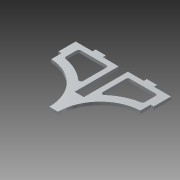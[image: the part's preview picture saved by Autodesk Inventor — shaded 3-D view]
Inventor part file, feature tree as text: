
AUTODESK INVENTOR PART (.ipt)
format: ipt  version: 2013 (Build 170138000, 138)  size: 154,624 bytes
history: native  units: mm
features: extrude x1, sketch x1
ambient origin geometry x8: Origin, YZ Plane, XZ Plane, XY Plane, X Axis, Y Axis, Z Axis, Center Point
feature tree (2):
  extrude  "Extrusion6"  Depth=3.0mm
  sketch  "Sketch1"  dims[d1=46.5mm d3=3.0mm d5=82.5mm d7=45.5mm d10=10.0mm d12=65.0mm d23=3.0mm d24=10.0mm d25=20.0mm d31=8.0mm d32=8.0mm d33=5.0mm d36=15.5mm d37=16.5mm d38=16.75mm d39=5.0mm d40=2.0mm d45=8.0mm d49=68.0mm d50=25.0mm d55=3.0mm d56=0.0mm]
